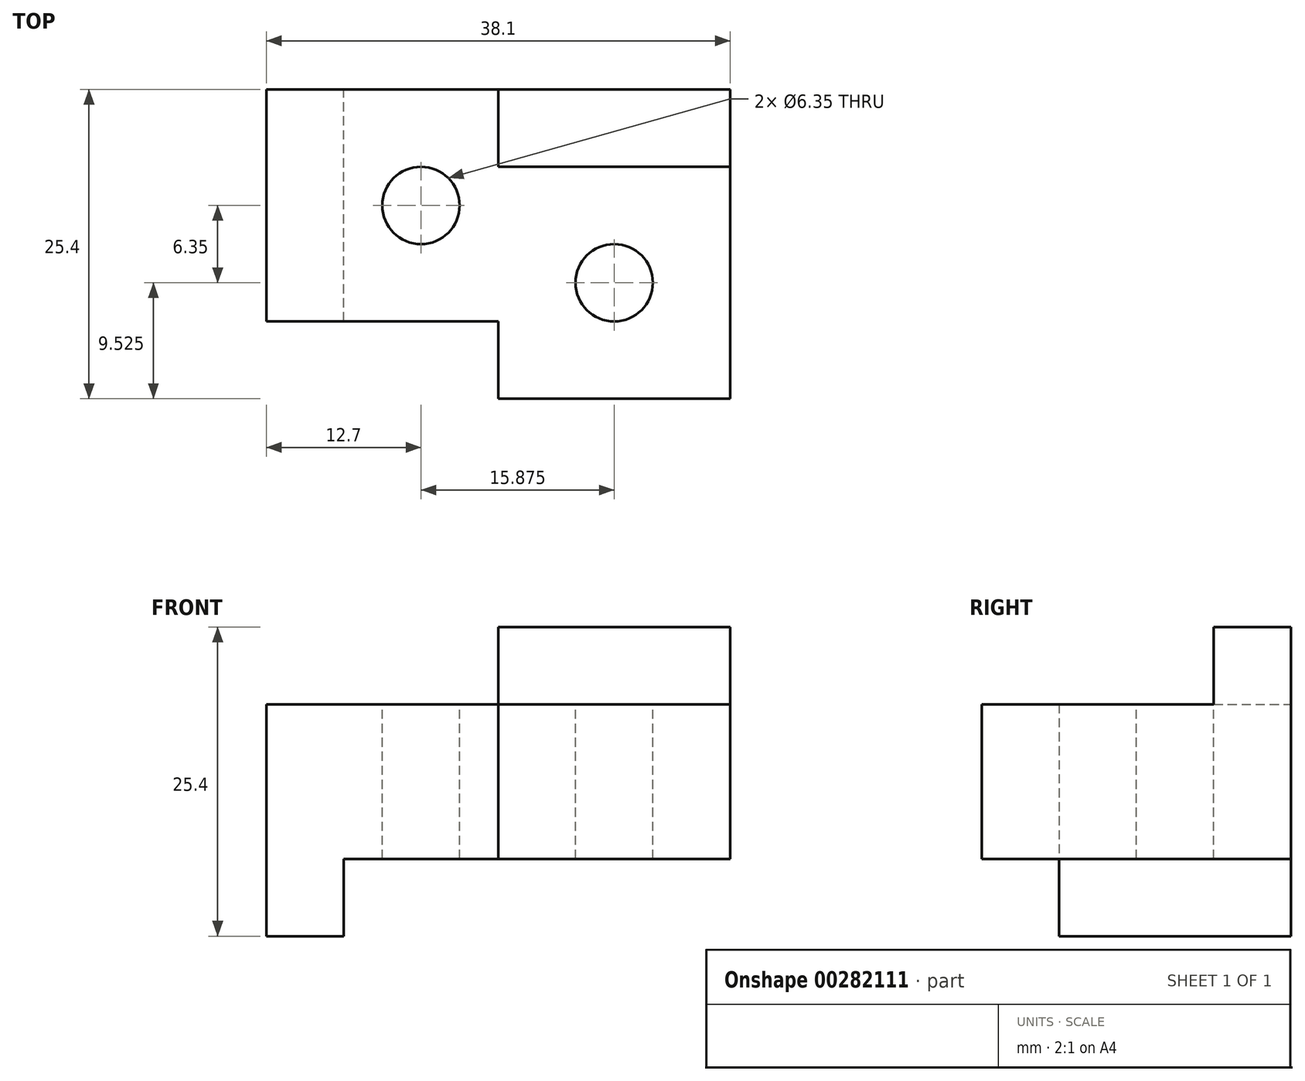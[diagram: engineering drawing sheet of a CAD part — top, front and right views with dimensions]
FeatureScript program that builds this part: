
annotation { "Feature Type Name" : "Feature", "Feature Type Description" : "" }
export const myFeature = defineFeature(function(context is Context, id is Id, definition is map)
    precondition{}
    {
        {
            var Q0;
            Q0=qCreatedBy(makeId("Top.planeOp"),FACE);
            var sketch = newSketch(context, id + "F0", { "sketchPlane" : qUnion([Q0])});
            skLineSegment(sketch, "E0", {"start": v(0, 0) * mm, "end": v(0, 19.05) * mm});
            skLineSegment(sketch, "E1", {"start": v(0, 19.05) * mm, "end": v(38.1, 19.05) * mm});
            skLineSegment(sketch, "E2", {"start": v(38.1, 19.05) * mm, "end": v(38.1, -6.35) * mm});
            skLineSegment(sketch, "E3", {"start": v(38.1, -6.35) * mm, "end": v(19.05, -6.35) * mm});
            skLineSegment(sketch, "E4", {"start": v(19.05, -6.35) * mm, "end": v(19.05, 0) * mm});
            skLineSegment(sketch, "E5", {"start": v(19.05, 0) * mm, "end": v(0, 0) * mm});
            skSolve(sketch);
        }
        {
            var Q0;
            Q0 = qSketchRegion(id + "F0", true);
            extrude(context, id + "F1", {"entities" : qUnion([Q0]), "depth" : 12.7 * mm});
        }
        {
            var Q0;
            Q0=makeQuery(id+"F1.opExtrude","CAP_FACE",FACE,{"disambiguationData":[OSD([sQuery(id+"F0.wireOp",EDGE,"E0"),sQuery(id+"F0.wireOp",EDGE,"E1"),sQuery(id+"F0.wireOp",EDGE,"E2"),sQuery(id+"F0.wireOp",EDGE,"E3"),sQuery(id+"F0.wireOp",EDGE,"E4"),sQuery(id+"F0.wireOp",EDGE,"E5")])],"isStart":true});
            var sketch = newSketch(context, id + "F2", { "sketchPlane" : qUnion([Q0])});
            skLineSegment(sketch, "E6", {"start": v(0, 0) * mm, "end": v(6.35, 0) * mm});
            skLineSegment(sketch, "E7", {"start": v(6.35, 0) * mm, "end": v(6.35, -19.05) * mm});
            skLineSegment(sketch, "E8", {"start": v(6.35, -19.05) * mm, "end": v(0, -19.05) * mm});
            skLineSegment(sketch, "E9", {"start": v(0, -19.05) * mm, "end": v(0, 0) * mm});
            skSolve(sketch);
        }
        {
            var Q0;
            Q0 = qSketchRegion(id + "F2", true);
            extrude(context, id + "F3", {"entities" : qUnion([Q0]), "operationType" : NewBodyOperationType.ADD, "depth" : 6.35 * mm});
        }
        {
            var Q0;
            Q0=makeQuery(id+"F1.opExtrude","CAP_FACE",FACE,{"disambiguationData":[OSD([sQuery(id+"F0.wireOp",EDGE,"E0"),sQuery(id+"F0.wireOp",EDGE,"E1"),sQuery(id+"F0.wireOp",EDGE,"E2"),sQuery(id+"F0.wireOp",EDGE,"E3"),sQuery(id+"F0.wireOp",EDGE,"E4"),sQuery(id+"F0.wireOp",EDGE,"E5")])],"isStart":false});
            var sketch = newSketch(context, id + "F4", { "sketchPlane" : qUnion([Q0])});
            skLineSegment(sketch, "E10", {"start": v(19.05, 0) * mm, "end": v(19.05, 19.05) * mm});
            skLineSegment(sketch, "E11", {"start": v(19.05, 12.7) * mm, "end": v(38.1, 12.7) * mm});
            skSolve(sketch);
        }
        {
            var Q0;
            {var subQ3=sQuery(id+"F4.wireOp",EDGE,"E11");Q0=makeQuery(id+"F4.imprint","IMPRINT",FACE,{"disambiguationData":[TD([[makeQuery(id+"F4.imprint","IMPRINT",EDGE,{"derivedFrom":subQ3}),1.0]])]});}
            extrude(context, id + "F5", {"entities" : qUnion([Q0]), "operationType" : NewBodyOperationType.ADD, "depth" : 6.35 * mm});
        }
        {
            var Q0;
            Q0=makeQuery(id+"F1.opExtrude","CAP_FACE",FACE,{"disambiguationData":[OSD([sQuery(id+"F0.wireOp",EDGE,"E0"),sQuery(id+"F0.wireOp",EDGE,"E1"),sQuery(id+"F0.wireOp",EDGE,"E2"),sQuery(id+"F0.wireOp",EDGE,"E3"),sQuery(id+"F0.wireOp",EDGE,"E4"),sQuery(id+"F0.wireOp",EDGE,"E5")])],"isStart":false});
            var sketch = newSketch(context, id + "F6", { "sketchPlane" : qUnion([Q0])});
            skLineSegment(sketch, "E12", {"start": v(0, 9.53) * mm, "end": v(19.05, 9.53) * mm, "construction": true});
            skCircle(sketch, "E13", {"center": v(12.7, 9.53) * mm, "radius": 3.18 * mm});
            skLineSegment(sketch, "E14", {"start": v(28.58, 12.7) * mm, "end": v(28.58, -6.35) * mm, "construction": true});
            skLineSegment(sketch, "E15", {"start": v(19.05, 3.17) * mm, "end": v(38.1, 3.18) * mm, "construction": true});
            skCircle(sketch, "E16", {"center": v(28.58, 3.17) * mm, "radius": 3.18 * mm});
            skLineSegment(sketch, "E17", {"start": v(12.7, 19.05) * mm, "end": v(12.7, 0) * mm, "construction": true});
            skSolve(sketch);
        }
        {
            var Q0;
            Q0=makeQuery(id+"F6.imprint","IMPRINT",FACE,{"disambiguationData":[TD([[makeQuery(id+"F6.imprint","IMPRINT",EDGE,{"derivedFrom":sQuery(id+"F6.wireOp",EDGE,"E16")}),1.0]])]});
            extrude(context, id + "F7", {"entities" : qUnion([Q0]), "operationType" : NewBodyOperationType.REMOVE, "oppositeDirection" : true, "depth" : 25.4 * mm});
        }
        {
            var Q0;
            Q0=makeQuery(id+"F6.imprint","IMPRINT",FACE,{"disambiguationData":[TD([[makeQuery(id+"F6.imprint","IMPRINT",EDGE,{"derivedFrom":sQuery(id+"F6.wireOp",EDGE,"E13")}),1.0]])]});
            extrude(context, id + "F8", {"entities" : qUnion([Q0]), "operationType" : NewBodyOperationType.REMOVE, "oppositeDirection" : true, "depth" : 25.4 * mm});
        }
    });
